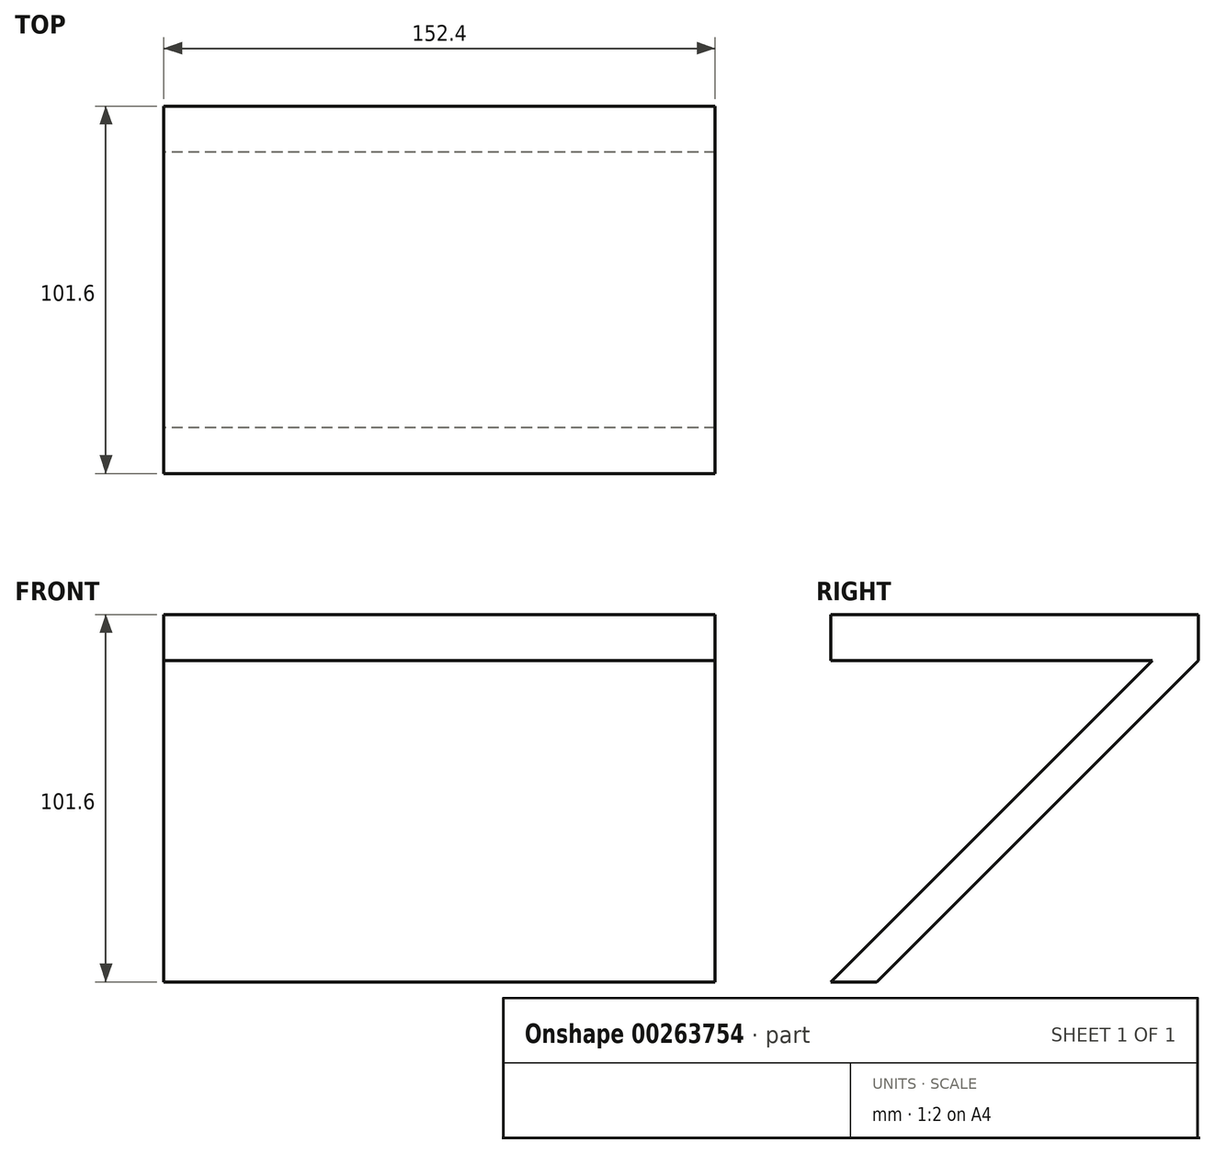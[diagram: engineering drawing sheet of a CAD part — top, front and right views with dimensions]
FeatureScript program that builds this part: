
annotation { "Feature Type Name" : "Feature", "Feature Type Description" : "" }
export const myFeature = defineFeature(function(context is Context, id is Id, definition is map)
    precondition{}
    {
        {
            var Q0;
            Q0=qCreatedBy(makeId("Top.planeOp"),FACE);
            var sketch = newSketch(context, id + "F0", { "sketchPlane" : qUnion([Q0])});
            skLineSegment(sketch, "E0.bottom", {"start": v(-74.55, 58.29) * mm, "end": v(77.85, 58.29) * mm});
            skLineSegment(sketch, "E0.top", {"start": v(-74.55, -43.31) * mm, "end": v(77.85, -43.31) * mm});
            skLineSegment(sketch, "E0.left", {"start": v(-74.55, 58.29) * mm, "end": v(-74.55, -43.31) * mm});
            skLineSegment(sketch, "E0.right", {"start": v(77.85, 58.29) * mm, "end": v(77.85, -43.31) * mm});
            skSolve(sketch);
        }
        {
            var Q0;
            Q0=makeQuery(id+"F0.imprint","IMPRINT",FACE,{"disambiguationData":[TD([[makeQuery(id+"F0.imprint","IMPRINT",EDGE,{"derivedFrom":sQuery(id+"F0.wireOp",EDGE,"E0.bottom")}),-1.0]])]});
            extrude(context, id + "F1", {"entities" : qUnion([Q0]), "depth" : 101.6 * mm});
        }
        {
            var Q0;
            Q0=makeQuery(id+"F1.opExtrude","SWEPT_FACE",FACE,{"disambiguationData":[OSD([sQuery(id+"F0.wireOp",EDGE,"E0.left")])]});
            var sketch = newSketch(context, id + "F2", { "sketchPlane" : qUnion([Q0])});
            skLineSegment(sketch, "E1", {"start": v(-58.29, 88.9) * mm, "end": v(30.61, 0) * mm});
            skLineSegment(sketch, "E2", {"start": v(-58.29, 88.9) * mm, "end": v(-45.59, 88.9) * mm});
            skLineSegment(sketch, "E3", {"start": v(-45.59, 88.9) * mm, "end": v(43.31, 0) * mm});
            skLineSegment(sketch, "E4", {"start": v(30.61, 0) * mm, "end": v(43.31, 0) * mm});
            skLineSegment(sketch, "E5", {"start": v(-45.59, 88.9) * mm, "end": v(43.31, 88.9) * mm});
            skSolve(sketch);
        }
        {
            var Q0;
            {var subQ0=sQuery(id+"F2.wireOp",EDGE,"E3");Q0=makeQuery(id+"F2.imprint","IMPRINT",FACE,{"disambiguationData":[TD([[makeQuery(id+"F2.imprint","IMPRINT",EDGE,{"derivedFrom":subQ0}),1.0]])]});}
            var Q1;
            {var subQ0=sQuery(id+"F2.wireOp",EDGE,"E1");Q1=makeQuery(id+"F2.imprint","IMPRINT",FACE,{"disambiguationData":[TD([[makeQuery(id+"F2.imprint","IMPRINT",EDGE,{"derivedFrom":subQ0}),-1.0]])]});}
            extrude(context, id + "F3", {"entities" : qUnion([Q0, Q1]), "operationType" : NewBodyOperationType.REMOVE, "oppositeDirection" : true, "depth" : 152.4 * mm});
        }
    });
